# Revit family: Haworth_Maari_Chair_StarBase
name_source: partatom
category: Furniture
revit_build: Autodesk Revit 2018 (Build: 20170223_1515(x64)
units: mm (PartAtom-declared; Revit-internal decimal feet)

## family parameters
Always vertical = Yes
Cut with Voids When Loaded = No
OmniClass Number = 23.40.70.14.64.21
OmniClass Title = Systems Furniture
Room Calculation Point = No
Shared = No
Work Plane-Based = No

## types (4) — shared parameters
Arm Cap Finish = Haworth _ Polymer _ Water TR-1W
Assembly Code = E2020200
Manufacturer = Haworth
Model = Haworth Maari
Revision Number = 2
Seat Pan Finish = Haworth _ Paint _ Black
Size = Verify Final Dim. w/ Haworth
Sustainability Info = https://www.haworth.com
URL = www.haworth.com
URL - Product = https://www.haworth.com
Warranty = http://www.haworth.com

## per-type parameters (varying)
| type | Actual Depth | Actual Height | Actual Width | Description | Five Star Base | Four Star Base | With Arms |
| S74 - Four Star Base - With Arms | 25 1/2" | 34" | 21 1/2" | Haworth Maari Chair - Four Star Base - With Arms | No | Yes | Yes |
| S75 - Five Star Base - With Arms | 28 1/2" | 32" | 28 1/2" | Haworth Maari Chair - Five Star Base - With Arms | Yes | No | Yes |
| S75 - Five Star Base - No Arms | 28 1/2" | 32" | 28 1/2" | Haworth Maari Chair - Five Star Base - No Arms | Yes | No | No |
| S74 - Four Star Base - No Arms | 25 1/2" | 34" | 21 1/2" | Haworth Maari Chair - Four Star Base - No Arms | No | Yes | No |

## geometry (parser evidence)
native form markers: Sweep x11
no freeform markers — native parametric forms only
